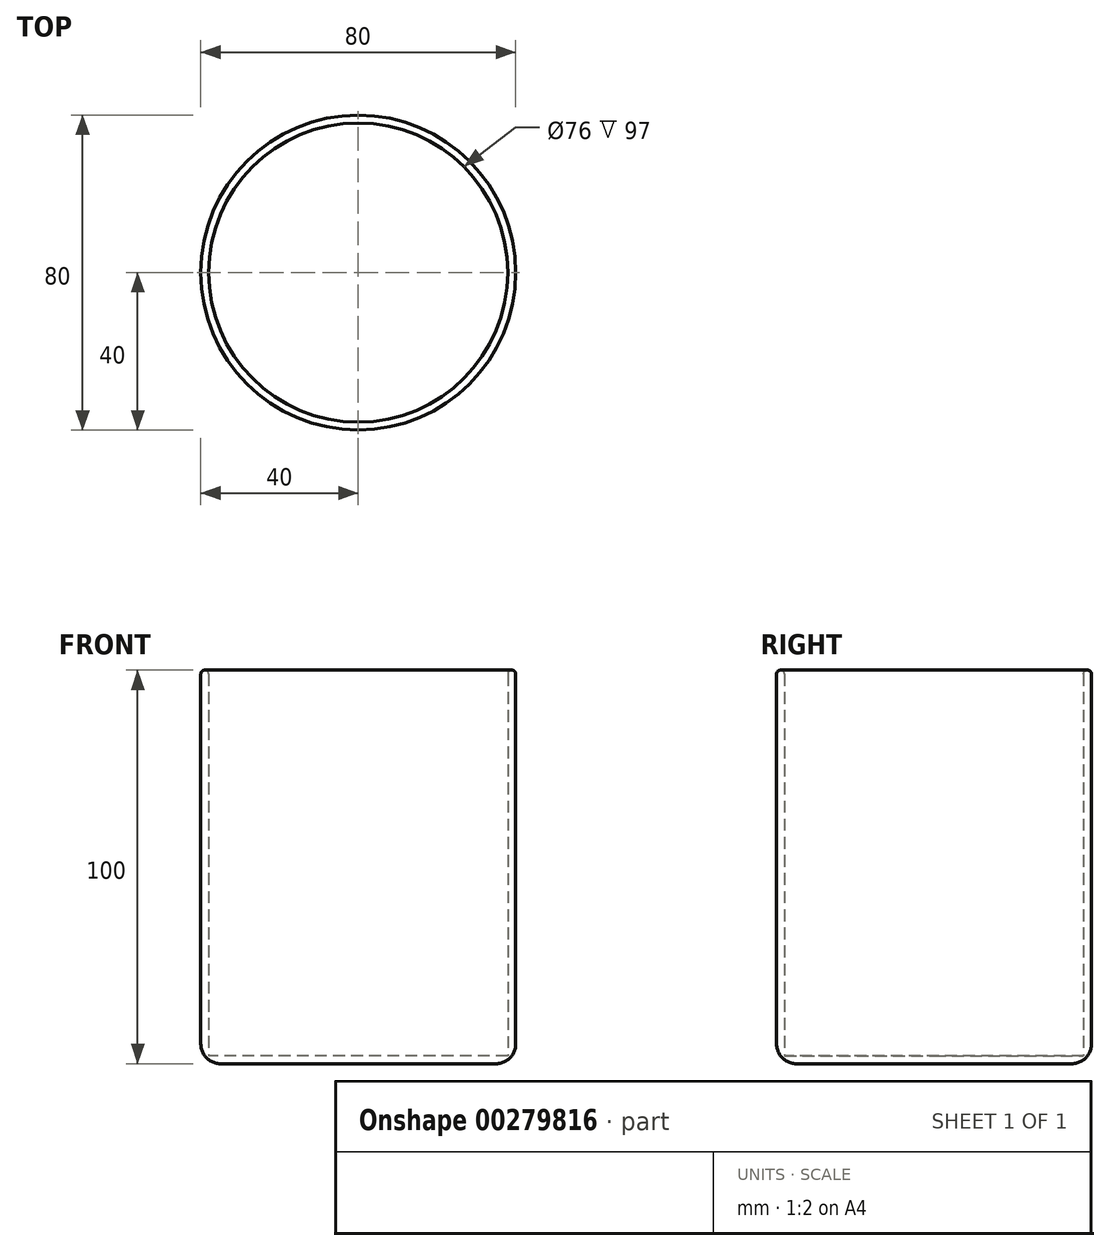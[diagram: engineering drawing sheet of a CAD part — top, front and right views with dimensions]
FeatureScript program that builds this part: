
annotation { "Feature Type Name" : "Feature", "Feature Type Description" : "" }
export const myFeature = defineFeature(function(context is Context, id is Id, definition is map)
    precondition{}
    {
        {
            var Q0;
            Q0=qCreatedBy(makeId("Top.planeOp"),FACE);
            var sketch = newSketch(context, id + "F0", { "sketchPlane" : qUnion([Q0])});
            skCircle(sketch, "E0", {"center": v(0, 0) * mm, "radius": 40 * mm});
            skSolve(sketch);
        }
        {
            var Q0;
            Q0=makeQuery(id+"F0.imprint","IMPRINT",FACE,{"disambiguationData":[TD([[makeQuery(id+"F0.imprint","IMPRINT",EDGE,{"derivedFrom":sQuery(id+"F0.wireOp",EDGE,"E0")}),1.0]])]});
            extrude(context, id + "F1", {"entities" : qUnion([Q0]), "depth" : 100 * mm});
        }
        {
            var Q0;
            Q0=makeQuery(id+"F1.opExtrude","CAP_FACE",FACE,{"disambiguationData":[OSD([sQuery(id+"F0.wireOp",EDGE,"E0")])],"isStart":false});
            shell(context, id + "F2", {"entities" : qUnion([Q0]), "thickness" : 2 * mm});
        }
        {
            var Q0;
            {var subQ0=sQuery(id+"F0.wireOp",EDGE,"E0");Q0=makeQuery(id+"F2.opShell","OFFSET_EDGE",EDGE,{"disambiguationData":[OSD([subQ0]),TDD([makeQuery(id+"F1.opExtrude","CAP_EDGE",EDGE,{"disambiguationData":[OSD([subQ0])],"isStart":false})])]});}
            fillet(context, id + "F3", {"entities" : qUnion([Q0]), "radius" : 1 * mm, "tangentPropagation" : true, "allowEdgeOverflow" : false});
        }
        {
            var Q0;
            Q0=makeQuery(id+"F1.opExtrude","CAP_EDGE",EDGE,{"disambiguationData":[OSD([sQuery(id+"F0.wireOp",EDGE,"E0")])],"isStart":false});
            fillet(context, id + "F4", {"entities" : qUnion([Q0]), "radius" : 1 * mm, "tangentPropagation" : true, "allowEdgeOverflow" : false});
        }
        {
            var Q0;
            Q0=makeQuery(id+"F1.opExtrude","CAP_EDGE",EDGE,{"disambiguationData":[OSD([sQuery(id+"F0.wireOp",EDGE,"E0")])],"isStart":true});
            fillet(context, id + "F5", {"entities" : qUnion([Q0]), "radius" : 5 * mm, "tangentPropagation" : true, "allowEdgeOverflow" : false});
        }
    });
